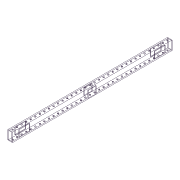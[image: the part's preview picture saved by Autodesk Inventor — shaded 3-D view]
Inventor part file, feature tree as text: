
AUTODESK INVENTOR PART (.ipt)
format: ipt  version: 2012 (Build 160160000, 160)  size: 190,976 bytes
history: native  units: in
note: dims shown in document units (in); Inventor stores cm internally (conversion verified against a paired STEP export)
features: extrude x3, sketch x3, pattern_linear x1
ambient origin geometry x8: Origin, YZ Plane, XZ Plane, XY Plane, X Axis, Y Axis, Z Axis, Center Point
bodies: Solid1 (feature_tree)
feature tree (7):
  extrude  "Extrusion1"  Depth=2.0in
  extrude  "Extrusion2"  Depth=0.125in
  extrude  "Extrusion3"  Depth=0.125in
  pattern_linear  "Rectangular Pattern1"  Spacing1=35.0in  [1 undecoded]
  sketch  "Sketch1"  dims[d0=1.0in d1=2.0in]
  sketch  "Sketch2"  dims[d2=0.125in d3=0.125in]
  sketch  "Sketch4"  dims[d4=0.125in d5=0.125in d6=35.0in d7=0.0in d8=1.5in d9=2.25in d10=0.25in d11=1.5in d12=37.0in d13=0.0in d14=1.5in d15=2.25in d16=1.5in d17=0.25in d19=0.25in d20=0.5in d21=0.5in d22=1.0in d23=0.0in d24=13.7795in d26=1.0in d27=1.5in d28=0.125in]
note: 1 required parameter value undecoded (feature->parameter linkage not recoverable at this tier; creation-order binding heuristic only, values carry confidence <= 0.55)
